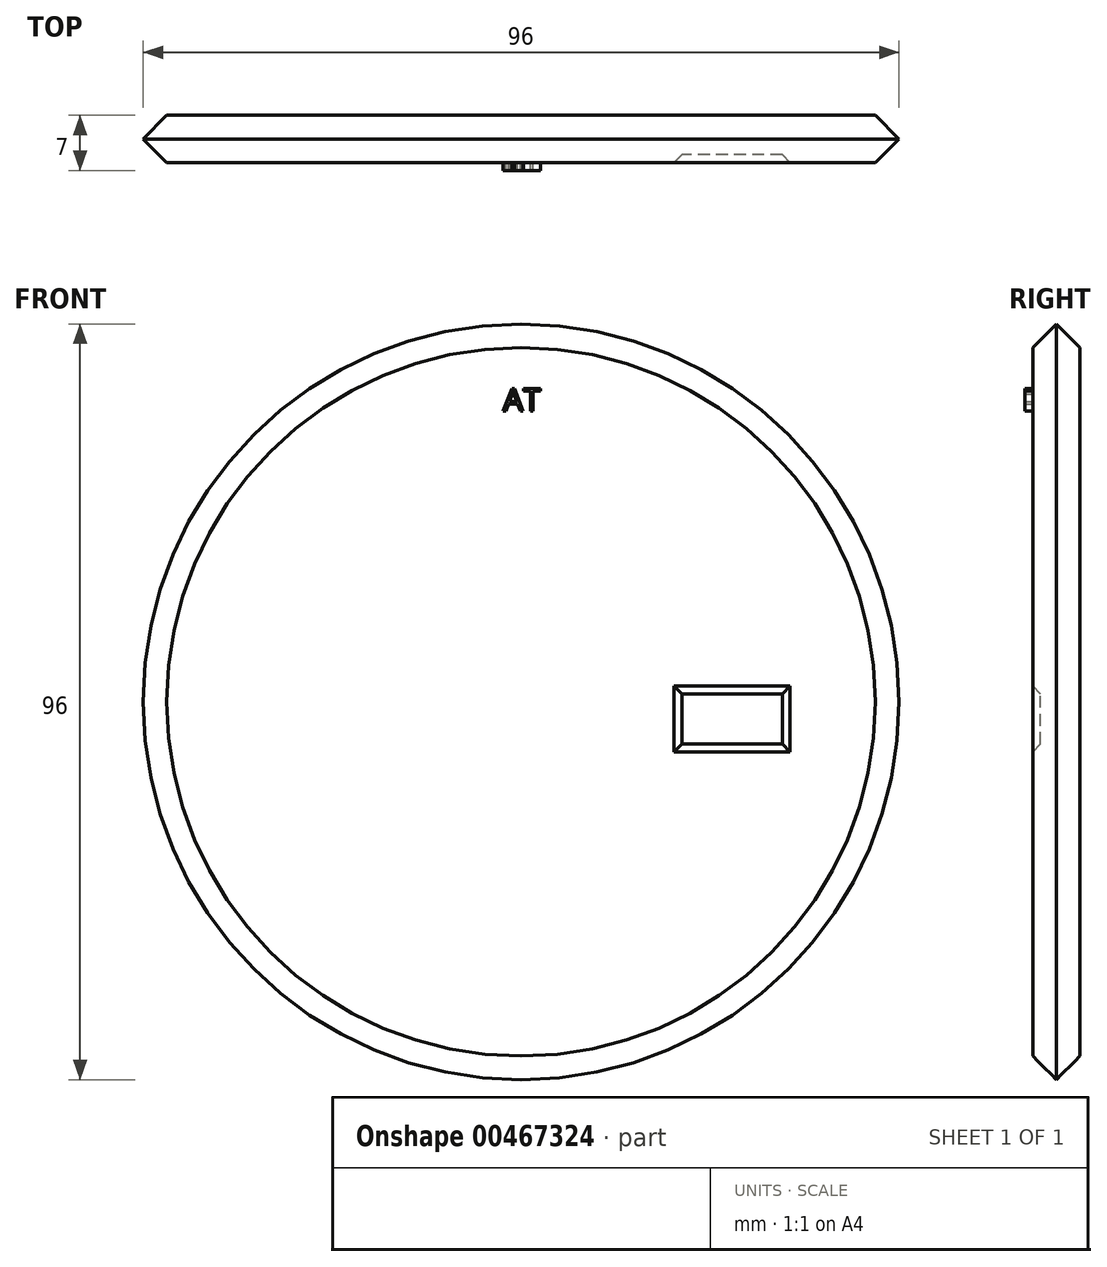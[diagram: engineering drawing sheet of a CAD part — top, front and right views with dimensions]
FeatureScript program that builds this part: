
annotation { "Feature Type Name" : "Feature", "Feature Type Description" : "" }
export const myFeature = defineFeature(function(context is Context, id is Id, definition is map)
    precondition{}
    {
        {
            var Q0;
            Q0=qCreatedBy(makeId("Front.planeOp"),FACE);
            var sketch = newSketch(context, id + "F0", { "sketchPlane" : qUnion([Q0])});
            skCircle(sketch, "E0", {"center": v(0, 0) * mm, "radius": 50 * mm});
            skSolve(sketch);
        }
        {
            var Q0;
            Q0 = qSketchRegion(id + "F0", true);
            extrude(context, id + "F1", {"entities" : qUnion([Q0]), "depth" : 5 * mm});
        }
        {
            var Q0;
            Q0=makeQuery(id+"F1.opExtrude","CAP_FACE",FACE,{"disambiguationData":[OSD([sQuery(id+"F0.wireOp",EDGE,"E0")])],"isStart":false});
            var sketch = newSketch(context, id + "F2", { "sketchPlane" : qUnion([Q0])});
            skLineSegment(sketch, "E1.bottom", {"start": v(21.43, 0) * mm, "end": v(32.18, 0) * mm});
            skLineSegment(sketch, "E1.top", {"start": v(21.43, -4.34) * mm, "end": v(32.18, -4.34) * mm});
            skLineSegment(sketch, "E1.left", {"start": v(21.43, 0) * mm, "end": v(21.43, -4.34) * mm});
            skLineSegment(sketch, "E1.right", {"start": v(32.18, 0) * mm, "end": v(32.18, -4.34) * mm});
            skSolve(sketch);
        }
        {
            var Q0;
            Q0=makeQuery(id+"F2.imprint","IMPRINT",FACE,{"disambiguationData":[TD([[makeQuery(id+"F2.imprint","IMPRINT",EDGE,{"derivedFrom":sQuery(id+"F2.wireOp",EDGE,"E1.bottom")}),1.0]])]});
            extrude(context, id + "F3", {"entities" : qUnion([Q0]), "operationType" : NewBodyOperationType.ADD, "depth" : 1 * mm});
        }
        {
            var Q0;
            Q0=makeQuery(id+"F3.opExtrude","CAP_EDGE",EDGE,{"disambiguationData":[OSD([sQuery(id+"F0.wireOp",EDGE,"E0")])],"isStart":false});
            chamfer(context, id + "F4", {"entities" : qUnion([Q0]), "width" : 5 * mm, "tangentPropagation" : true});
        }
        {
            var Q0;
            Q0=makeQuery(id+"F3.opExtrude","CAP_EDGE",EDGE,{"disambiguationData":[OSD([sQuery(id+"F2.wireOp",EDGE,"E1.top")])],"isStart":false});
            var Q1;
            Q1=makeQuery(id+"F3.opExtrude","CAP_EDGE",EDGE,{"disambiguationData":[OSD([sQuery(id+"F2.wireOp",EDGE,"E1.left")])],"isStart":false});
            var Q2;
            Q2=makeQuery(id+"F3.opExtrude","CAP_EDGE",EDGE,{"disambiguationData":[OSD([sQuery(id+"F2.wireOp",EDGE,"E1.bottom")])],"isStart":false});
            var Q3;
            Q3=makeQuery(id+"F3.opExtrude","CAP_EDGE",EDGE,{"disambiguationData":[OSD([sQuery(id+"F2.wireOp",EDGE,"E1.right")])],"isStart":false});
            chamfer(context, id + "F5", {"entities" : qUnion([Q0, Q1, Q2, Q3]), "width" : 2 * mm, "tangentPropagation" : true});
        }
        {
            var Q0;
            Q0=makeQuery(id+"F1.opExtrude","CAP_EDGE",EDGE,{"disambiguationData":[OSD([sQuery(id+"F0.wireOp",EDGE,"E0")])],"isStart":true});
            chamfer(context, id + "F6", {"entities" : qUnion([Q0]), "width" : 5 * mm, "tangentPropagation" : true});
        }
        {
            var Q0;
            Q0=makeQuery(id+"F3.opExtrude","CAP_FACE",FACE,{"disambiguationData":[OSD([sQuery(id+"F0.wireOp",EDGE,"E0"),sQuery(id+"F2.wireOp",EDGE,"E1.bottom"),sQuery(id+"F2.wireOp",EDGE,"E1.top"),sQuery(id+"F2.wireOp",EDGE,"E1.left"),sQuery(id+"F2.wireOp",EDGE,"E1.right")])],"isStart":false});
            var sketch = newSketch(context, id + "F7", { "sketchPlane" : qUnion([Q0])});
            skText(sketch, "E2", { "text": "AT", "fontName": "OpenSans-Regular.ttf"});
            skLineSegment(sketch, "E3", {"start": v(0, 19.26) * mm, "end": v(0, -19.83) * mm});
            const initialGuessF7  = {"E2": [-0.00228, 0.03692, 1, 0, 0.0029]};
            skSetInitialGuess(sketch, initialGuessF7);
            skSolve(sketch);
        }
        {
            var Q0;
            Q0 = qSketchRegion(id + "F7", true);
            extrude(context, id + "F8", {"entities" : qUnion([Q0]), "operationType" : NewBodyOperationType.ADD, "depth" : 1 * mm});
        }
    });
